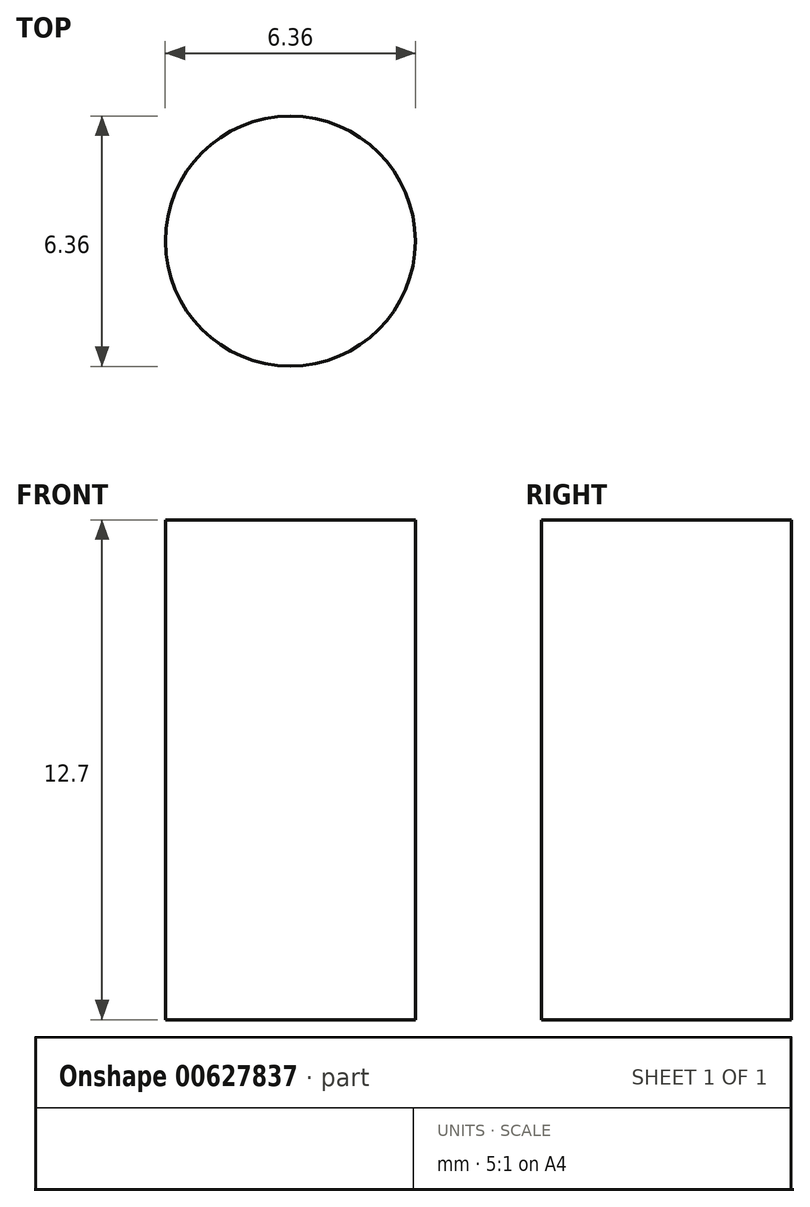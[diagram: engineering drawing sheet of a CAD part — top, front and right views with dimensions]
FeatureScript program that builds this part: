
annotation { "Feature Type Name" : "Feature", "Feature Type Description" : "" }
export const myFeature = defineFeature(function(context is Context, id is Id, definition is map)
    precondition{}
    {
        {
            var Q0;
            Q0=qCreatedBy(makeId("Top.planeOp"),FACE);
            var sketch = newSketch(context, id + "F0", { "sketchPlane" : qUnion([Q0])});
            skCircle(sketch, "E0", {"center": v(0, 0) * mm, "radius": 3.18 * mm});
            skSolve(sketch);
        }
        {
            var Q0;
            Q0 = qSketchRegion(id + "F0", true);
            extrude(context, id + "F1", {"entities" : qUnion([Q0]), "depth" : 12.7 * mm, "offsetDistance" : 25.4 * mm});
        }
    });
